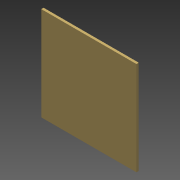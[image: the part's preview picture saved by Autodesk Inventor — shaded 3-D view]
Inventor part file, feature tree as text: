
AUTODESK INVENTOR PART (.ipt)
format: ipt  version: 2015 (Build 190159000, 159)  size: 81,408 bytes
history: native  units: mm
features: other x1, extrude x1, sketch x1
ambient origin geometry x8: Origin, YZ Plane, XZ Plane, XY Plane, X Axis, Y Axis, Z Axis, Center Point
bodies: Body1 (feature_tree)
feature tree (3):
  other  "Bryła1"
  extrude  "Wyciągnięcie proste1"  Depth=405.0mm
  sketch  "Szkic1"
